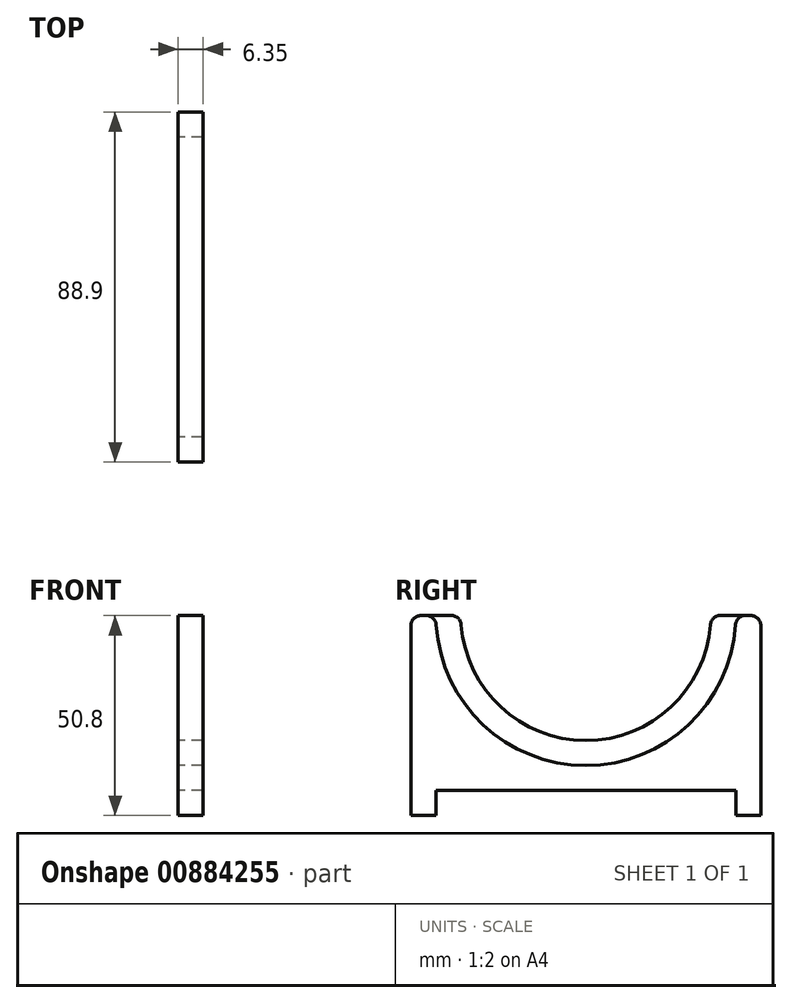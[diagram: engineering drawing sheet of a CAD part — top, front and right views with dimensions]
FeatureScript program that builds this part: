
annotation { "Feature Type Name" : "Feature", "Feature Type Description" : "" }
export const myFeature = defineFeature(function(context is Context, id is Id, definition is map)
    precondition{}
    {
        {
            var Q0;
            Q0=qCreatedBy(makeId("Right.planeOp"),FACE);
            var sketch = newSketch(context, id + "F0", { "sketchPlane" : qUnion([Q0])});
            skLineSegment(sketch, "E0.bottom", {"start": v(-41.9, 0) * mm, "end": v(-34.2, 0) * mm});
            skLineSegment(sketch, "E0.top", {"start": v(-44.45, -44.45) * mm, "end": v(-44.45, -44.45) * mm});
            skLineSegment(sketch, "E0.left", {"start": v(-44.45, -2.54) * mm, "end": v(-44.45, -44.45) * mm});
            skLineSegment(sketch, "E0.right", {"start": v(44.45, -2.54) * mm, "end": v(44.45, -44.45) * mm});
            skArc(sketch, "E1", {"start": v(-31.66, -2.35) * mm, "mid": v(0, -31.75) * mm, "end": v(31.66, -2.35) * mm});
            skLineSegment(sketch, "E2.trimOffspring", {"start": v(34.2, 0) * mm, "end": v(41.9, 0) * mm});
            skLineSegment(sketch, "E3.top", {"start": v(-44.45, -50.8) * mm, "end": v(-38.1, -50.8) * mm});
            skLineSegment(sketch, "E3.left", {"start": v(-44.45, -44.45) * mm, "end": v(-44.45, -50.8) * mm});
            skLineSegment(sketch, "E3.right", {"start": v(-38.1, -44.45) * mm, "end": v(-38.1, -50.8) * mm});
            skLineSegment(sketch, "E4.top", {"start": v(38.09, -50.78) * mm, "end": v(44.44, -50.78) * mm});
            skLineSegment(sketch, "E4.left", {"start": v(38.09, -44.43) * mm, "end": v(38.09, -50.78) * mm});
            skLineSegment(sketch, "E4.right", {"start": v(44.44, -44.43) * mm, "end": v(44.44, -50.78) * mm});
            skLineSegment(sketch, "E5.trimOffspring", {"start": v(-38.1, -44.45) * mm, "end": v(38.09, -44.45) * mm});
            skLineSegment(sketch, "E6.trimOffspring", {"start": v(44.44, -44.45) * mm, "end": v(44.45, -44.45) * mm});
            skPoint(sketch, "E7.visualSharp", {"position": v(-44.45, 0) * mm});
            skArc(sketch, "E7.filletArc", {"start": v(-41.9, 0) * mm, "mid": v(-43.7, -0.74) * mm, "end": v(-44.45, -2.54) * mm});
            skPoint(sketch, "E8.visualSharp", {"position": v(-31.75, 0) * mm});
            skArc(sketch, "E8.filletArc", {"start": v(-31.66, -2.35) * mm, "mid": v(-32.47, -0.68) * mm, "end": v(-34.2, 0) * mm});
            skPoint(sketch, "E9.visualSharp", {"position": v(31.75, 0) * mm});
            skArc(sketch, "E9.filletArc", {"start": v(34.2, 0) * mm, "mid": v(32.47, -0.68) * mm, "end": v(31.66, -2.35) * mm});
            skPoint(sketch, "E10.visualSharp", {"position": v(44.45, 0) * mm});
            skArc(sketch, "E10.filletArc", {"start": v(44.45, -2.54) * mm, "mid": v(43.7, -0.74) * mm, "end": v(41.91, 0) * mm});
            skSolve(sketch);
        }
        {
            var Q0;
            Q0=makeQuery(id+"F0.imprint","IMPRINT",FACE,{"disambiguationData":[TD([[makeQuery(id+"F0.imprint","IMPRINT",EDGE,{"derivedFrom":sQuery(id+"F0.wireOp",EDGE,"E0.bottom")}),-1.0]])]});
            extrude(context, id + "F1", {"entities" : qUnion([Q0]), "depth" : 6.35 * mm, "offsetDistance" : 25.4 * mm});
        }
        {
            var Q0;
            Q0=qCreatedBy(makeId("Right.planeOp"),FACE);
            var sketch = newSketch(context, id + "F2", { "sketchPlane" : qUnion([Q0])});
            skLineSegment(sketch, "E11.bottom", {"start": v(-41.9, 0) * mm, "end": v(-34.2, 0) * mm});
            skLineSegment(sketch, "E11.top", {"start": v(-44.45, -50.8) * mm, "end": v(-38.1, -50.8) * mm});
            skLineSegment(sketch, "E11.left", {"start": v(-44.45, -2.54) * mm, "end": v(-44.45, -50.8) * mm});
            skLineSegment(sketch, "E11.right", {"start": v(44.45, -2.54) * mm, "end": v(44.45, -50.8) * mm});
            skArc(sketch, "E12", {"start": v(-31.66, -2.35) * mm, "mid": v(0, -31.75) * mm, "end": v(31.66, -2.35) * mm});
            skLineSegment(sketch, "E13.trimOffspring", {"start": v(34.2, 0) * mm, "end": v(41.9, 0) * mm});
            skLineSegment(sketch, "E14.top", {"start": v(-38.1, -44.45) * mm, "end": v(38.1, -44.45) * mm});
            skLineSegment(sketch, "E14.left", {"start": v(-38.1, -50.8) * mm, "end": v(-38.1, -44.45) * mm});
            skLineSegment(sketch, "E14.right", {"start": v(38.1, -50.8) * mm, "end": v(38.1, -44.45) * mm});
            skLineSegment(sketch, "E15.trimOffspring", {"start": v(38.1, -50.8) * mm, "end": v(44.45, -50.8) * mm});
            skPoint(sketch, "E16.visualSharp", {"position": v(-44.45, 0) * mm});
            skArc(sketch, "E16.filletArc", {"start": v(-41.9, 0) * mm, "mid": v(-43.7, -0.74) * mm, "end": v(-44.45, -2.54) * mm});
            skPoint(sketch, "E17.visualSharp", {"position": v(-31.75, 0) * mm});
            skArc(sketch, "E17.filletArc", {"start": v(-31.66, -2.35) * mm, "mid": v(-32.47, -0.68) * mm, "end": v(-34.2, 0) * mm});
            skPoint(sketch, "E18.visualSharp", {"position": v(31.75, 0) * mm});
            skArc(sketch, "E18.filletArc", {"start": v(34.2, 0) * mm, "mid": v(32.47, -0.68) * mm, "end": v(31.66, -2.35) * mm});
            skPoint(sketch, "E19.visualSharp", {"position": v(44.45, 0) * mm});
            skArc(sketch, "E19.filletArc", {"start": v(44.45, -2.54) * mm, "mid": v(43.7, -0.74) * mm, "end": v(41.9, 0) * mm});
            skSolve(sketch);
        }
        {
            var Q0;
            Q0=makeQuery(id+"F2.imprint","IMPRINT",FACE,{"disambiguationData":[TD([[makeQuery(id+"F2.imprint","IMPRINT",EDGE,{"derivedFrom":sQuery(id+"F2.wireOp",EDGE,"E11.bottom")}),-1.0]])]});
            extrude(context, id + "F3", {"entities" : qUnion([Q0]), "depth" : 6.35 * mm, "offsetDistance" : 25.4 * mm});
        }
        {
            var Q0;
            Q0=qCreatedBy(makeId("Right.planeOp"),FACE);
            var sketch = newSketch(context, id + "F4", { "sketchPlane" : qUnion([Q0])});
            skLineSegment(sketch, "E20.bottom", {"start": v(-41.9, 0) * mm, "end": v(-40.56, 0) * mm});
            skLineSegment(sketch, "E20.top", {"start": v(-38.1, -44.45) * mm, "end": v(38.1, -44.45) * mm});
            skLineSegment(sketch, "E20.left", {"start": v(-44.45, -2.54) * mm, "end": v(-44.45, -44.45) * mm});
            skLineSegment(sketch, "E20.right", {"start": v(44.45, -2.54) * mm, "end": v(44.45, -44.45) * mm});
            skArc(sketch, "E21", {"start": v(-38.03, -2.38) * mm, "mid": v(0, -38.1) * mm, "end": v(38.03, -2.38) * mm});
            skLineSegment(sketch, "E22.trimOffspring", {"start": v(40.56, 0) * mm, "end": v(41.91, 0) * mm});
            skLineSegment(sketch, "E23.top", {"start": v(-44.45, -50.8) * mm, "end": v(-38.1, -50.8) * mm});
            skLineSegment(sketch, "E23.left", {"start": v(-44.45, -44.45) * mm, "end": v(-44.45, -50.8) * mm});
            skLineSegment(sketch, "E23.right", {"start": v(-38.1, -44.45) * mm, "end": v(-38.1, -50.8) * mm});
            skLineSegment(sketch, "E24.top", {"start": v(44.45, -50.8) * mm, "end": v(38.1, -50.8) * mm});
            skLineSegment(sketch, "E24.left", {"start": v(44.45, -44.45) * mm, "end": v(44.45, -50.8) * mm});
            skLineSegment(sketch, "E24.right", {"start": v(38.1, -44.45) * mm, "end": v(38.1, -50.8) * mm});
            skPoint(sketch, "E25.visualSharp", {"position": v(-44.45, 0) * mm});
            skArc(sketch, "E25.filletArc", {"start": v(-41.9, 0) * mm, "mid": v(-43.7, -0.74) * mm, "end": v(-44.45, -2.54) * mm});
            skPoint(sketch, "E26.visualSharp", {"position": v(-38.1, 0) * mm});
            skArc(sketch, "E26.filletArc", {"start": v(-38.03, -2.38) * mm, "mid": v(-38.82, -0.69) * mm, "end": v(-40.56, 0) * mm});
            skPoint(sketch, "E27.visualSharp", {"position": v(38.1, 0) * mm});
            skArc(sketch, "E27.filletArc", {"start": v(40.56, 0) * mm, "mid": v(38.82, -0.69) * mm, "end": v(38.03, -2.38) * mm});
            skPoint(sketch, "E28.visualSharp", {"position": v(44.45, 0) * mm});
            skArc(sketch, "E28.filletArc", {"start": v(44.45, -2.54) * mm, "mid": v(43.7, -0.74) * mm, "end": v(41.91, 0) * mm});
            skSolve(sketch);
        }
        {
            var Q0;
            Q0=makeQuery(id+"F1.opExtrude","SWEPT_BODY",BODY,{"disambiguationData":[OSD([sQuery(id+"F0.wireOp",EDGE,"E0.bottom"),sQuery(id+"F0.wireOp",EDGE,"E0.top"),sQuery(id+"F0.wireOp",EDGE,"E0.left"),sQuery(id+"F0.wireOp",EDGE,"E0.right"),sQuery(id+"F0.wireOp",EDGE,"E1"),sQuery(id+"F0.wireOp",EDGE,"E2.trimOffspring"),sQuery(id+"F0.wireOp",EDGE,"E3.top"),sQuery(id+"F0.wireOp",EDGE,"E3.left"),sQuery(id+"F0.wireOp",EDGE,"E3.right"),sQuery(id+"F0.wireOp",EDGE,"E4.top"),sQuery(id+"F0.wireOp",EDGE,"E4.left"),sQuery(id+"F0.wireOp",EDGE,"E4.right"),sQuery(id+"F0.wireOp",EDGE,"E5.trimOffspring"),sQuery(id+"F0.wireOp",EDGE,"E6.trimOffspring"),sQuery(id+"F0.wireOp",EDGE,"E7.filletArc"),sQuery(id+"F0.wireOp",EDGE,"E8.filletArc"),sQuery(id+"F0.wireOp",EDGE,"E9.filletArc"),sQuery(id+"F0.wireOp",EDGE,"E10.filletArc")])]});
            deleteBodies(context, id + "F5", {"entities" : qUnion([Q0])});
        }
        {
            var Q0;
            Q0=makeQuery(id+"F4.imprint","IMPRINT",FACE,{"disambiguationData":[TD([[makeQuery(id+"F4.imprint","IMPRINT",EDGE,{"derivedFrom":sQuery(id+"F4.wireOp",EDGE,"E20.bottom")}),-1.0]])]});
            extrude(context, id + "F6", {"entities" : qUnion([Q0]), "depth" : 6.35 * mm, "offsetDistance" : 25.4 * mm});
        }
    });
